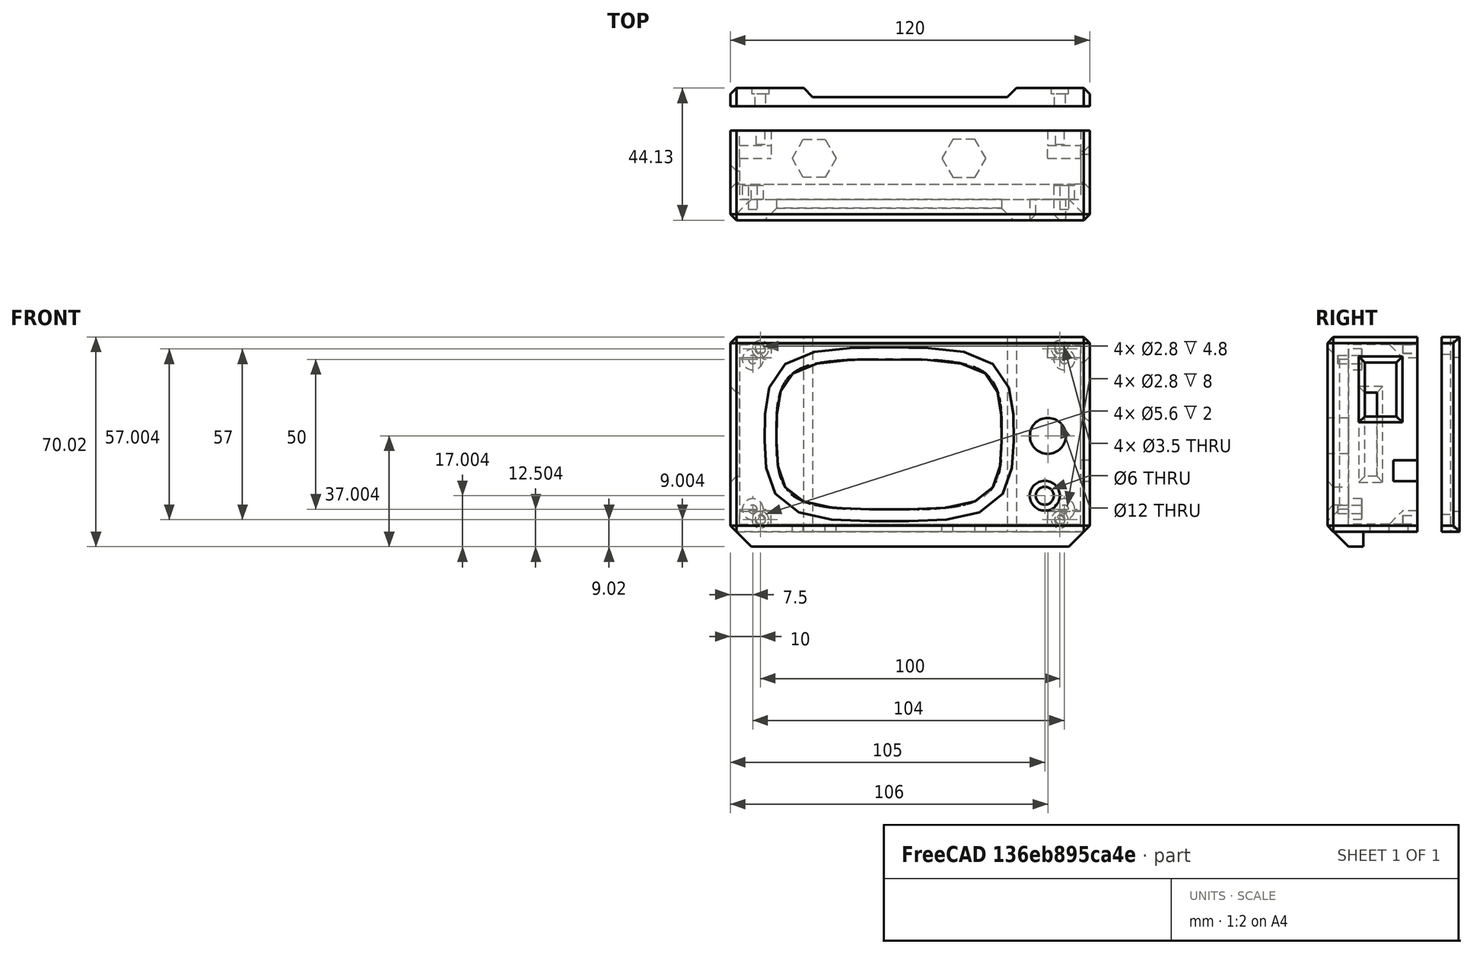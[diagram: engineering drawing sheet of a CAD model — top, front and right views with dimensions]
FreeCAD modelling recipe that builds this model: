
FCSTD DOCUMENT  (FreeCAD 0.19R)
Label: Pendant
License: All rights reserved
LicenseURL: http://en.wikipedia.org/wiki/All_rights_reserved
objects: Sketcher::SketchObject×18, PartDesign::Pocket×12, PartDesign::Chamfer×8, PartDesign::Pad×5, PartDesign::Mirrored×2, PartDesign::Body×2, Mesh::Feature×2
note: 72 computed .brp shape members not serialized (recipe doc carries the construction recipe); baked Part::Feature solids carry a one-line shape summary decoded from their .brp

FEATURE [Sketcher::SketchObject] Sketch028  label="knob"
  FullyConstrained = false
  MapMode = 5
  Placement = pos=(0,0,0) rot=(1,0,0;3.14159rad)
  sketch-geometry (1):
    g0: Circle CenterX=52 CenterY=20.5 CenterZ=0 NormalX=0 NormalY=0 NormalZ=1 AngleXU=0 Radius=3
  constraints (1):
    c: Diameter(g0) = 6
FEATURE [Sketcher::SketchObject] Sketch029
  FullyConstrained = true
  MapMode = 5
  Support = -> [XY_Plane002]
  sketch-geometry (30):
    g0: LineSegment StartX=-53 StartY=32.5 StartZ=0 EndX=67 EndY=32.5 EndZ=0
    g1: LineSegment StartX=67 StartY=32.5 StartZ=0 EndX=67 EndY=-32.5 EndZ=0
    g2: LineSegment StartX=67 StartY=-32.5 StartZ=0 EndX=-53 EndY=-32.5 EndZ=0
    g3: LineSegment StartX=-53 StartY=-32.5 StartZ=0 EndX=-53 EndY=32.5 EndZ=0
    g4: LineSegment StartX=-37 StartY=24.5 StartZ=0 EndX=37 EndY=24.5 EndZ=0
    g5: LineSegment StartX=37 StartY=24.5 StartZ=0 EndX=37 EndY=-24.5 EndZ=0
    g6: LineSegment StartX=37 StartY=-24.5 StartZ=0 EndX=-37 EndY=-24.5 EndZ=0
    g7: LineSegment StartX=-37 StartY=-24.5 StartZ=0 EndX=-37 EndY=24.5 EndZ=0
    g8: LineSegment StartX=-37.7408 StartY=25.116 StartZ=0 EndX=37.7408 EndY=25.116 EndZ=0
    g9: LineSegment StartX=37.7408 StartY=25.116 StartZ=0 EndX=37.7408 EndY=-25.116 EndZ=0
    g10: LineSegment StartX=37.7408 StartY=-25.116 StartZ=0 EndX=-37.7408 EndY=-25.116 EndZ=0
    g11: LineSegment StartX=-37.7408 StartY=-25.116 StartZ=0 EndX=-37.7408 EndY=25.116 EndZ=0
    g12-g19: Circle x8 (B-spline internal-alignment scaffolding for g20; pole/knot coordinates omitted)
    g20: BSplineCurve PolesCount=8 KnotsCount=9 Degree=3 IsPeriodic=1
    g21-g29: GeomPoint x9 (B-spline internal-alignment scaffolding for g20; pole/knot coordinates omitted)
  constraints (53):
    c: Coincident(g0,g1)
    c: Coincident(g1,g2)
    c: Coincident(g2,g3)
    c: Coincident(g3,g0)
    c: Horizontal(g0)
    c: Horizontal(g2)
    c: Vertical(g1)
    c: Vertical(g3)
    c: Coincident(g4,g5)
    c: Coincident(g5,g6)
    c: Coincident(g6,g7)
    c: Coincident(g7,g4)
    c: Horizontal(g4)
    c: Vertical(g7)
    c: Distance(g5) = 49
    c: Distance(g4,g3) = 16
    c: Distance(g0,g5) = 30
    c: Distance(g6,g2) = 8
    c: Distance(g4,g0) = 8
    c: Distance(g6) = 74
    c: Symmetric(g5,g6,g-2)
    c: Symmetric(g5,g4,g-1)
    c: Coincident(g8,g9)
    c: Coincident(g9,g10)
    c: Coincident(g10,g11)
    c: Coincident(g11,g8)
    c: Horizontal(g8)
    c: Horizontal(g10)
    c: Vertical(g9)
    c: Vertical(g11)
    c: Symmetric(g9,g8,g-1)
    c: Weight(g12) = 1
    c: Equal(g12,g13)
    c: Equal(g12,g14)
    c: Equal(g12,g15)
    c: PointOnObject(g15,g-1)
    c: Equal(g12,g16)
    c: Equal(g12,g17)
    c: PointOnObject(g17,g-2)
    c: Equal(g12,g18)
    c: Equal(g12,g19)
    c: InternalAlignment(g12-g19 -> g20) x8
    c: InternalAlignment(g21-g29 -> g20) x9
    c: Coincident(g8,g12)
    c: Coincident(g14,g8)
    c: Coincident(g16,g10)
    c: Coincident(g18,g9)
    c: Distance(g19,g5) = 0.5
    c: Symmetric(g19,g15,g-2)
    c: Distance(g17,g6) = 0.5
    c: Symmetric(g17,g13,g-1)
    c: DistanceX(g8) = 37.7408
    c: DistanceY(g8) = 25.116
FEATURE [PartDesign::Pad] Pad005
  Direction = (1,1,1)
  Length = 30
  Length2 = 100
  Profile = -> Sketch029
  Type = 0
FEATURE [PartDesign::Pocket] Pocket016
  BaseFeature = -> Pad005
  Length = 5
  Length2 = 100
  Profile = -> Sketch028
  Type = 1
FEATURE [Sketcher::SketchObject] Sketch001  label="knob001"
  FullyConstrained = false
  MapMode = 5
  Placement = pos=(0,0,30) rot=(0,0,1;0rad)
  Support = -> [Pocket016]
  sketch-geometry (1):
    g0: Circle CenterX=53 CenterY=-0.5 CenterZ=0 NormalX=0 NormalY=0 NormalZ=1 AngleXU=0 Radius=6
  constraints (2):
    c: Diameter(g0) = 12
    c: DistanceY(g0) = -0.5
FEATURE [PartDesign::Pocket] Pocket017
  BaseFeature = -> Pocket016
  Length = 5
  Length2 = 100
  Profile = -> Sketch001
  Type = 1
FEATURE [Sketcher::SketchObject] Sketch030  label="BodyPocket"
  ExternalGeometry = -> [Pocket017]
  FullyConstrained = true
  MapMode = 5
  Placement = pos=(0,0,0) rot=(1,0,0;3.14159rad)
  Support = -> [Pocket017]
  sketch-geometry (4):
    g0: LineSegment StartX=-50 StartY=30 StartZ=0 EndX=64 EndY=30 EndZ=0
    g1: LineSegment StartX=64 StartY=30 StartZ=0 EndX=64 EndY=-30 EndZ=0
    g2: LineSegment StartX=64 StartY=-30 StartZ=0 EndX=-50 EndY=-30 EndZ=0
    g3: LineSegment StartX=-50 StartY=-30 StartZ=0 EndX=-50 EndY=30 EndZ=0
  constraints (12):
    c: Coincident(g0,g1)
    c: Coincident(g1,g2)
    c: Coincident(g2,g3)
    c: Coincident(g3,g0)
    c: Horizontal(g0)
    c: Horizontal(g2)
    c: Vertical(g1)
    c: DistanceX(g0) = -50
    c: DistanceY(g0) = 30
    c: DistanceX(g1) = 64
    c: DistanceY(g2) = -30
    c: Vertical(g3)
FEATURE [PartDesign::Pocket] Pocket018
  BaseFeature = -> Pocket017
  Length = 23
  Length2 = 100
  Profile = -> Sketch030
  Type = 0
FEATURE [PartDesign::Chamfer] Chamfer001
  Angle = 45
  Base = -> Pocket018 [Edge19]
  BaseFeature = -> Pocket018
  ChamferType = 0
  FlipDirection = false
  Size = 4
  Size2 = 1
  SupportTransform = false
FEATURE [Sketcher::SketchObject] Sketch031  label="standofs"
  FullyConstrained = true
  MapMode = 5
  Placement = pos=(0,0,23) rot=(1,0,0;3.14159rad)
  Support = -> [Chamfer001]
  sketch-geometry (4):
    g0: Circle CenterX=-45.5 CenterY=25 CenterZ=0 NormalX=0 NormalY=0 NormalZ=1 AngleXU=0 Radius=3.5
    g1: Circle CenterX=-45.5 CenterY=-25 CenterZ=0 NormalX=0 NormalY=0 NormalZ=1 AngleXU=0 Radius=3.5
    g2: Circle CenterX=58.5 CenterY=-25 CenterZ=0 NormalX=0 NormalY=0 NormalZ=1 AngleXU=0 Radius=3.5
    g3: Circle CenterX=58.5 CenterY=25 CenterZ=0 NormalX=0 NormalY=0 NormalZ=1 AngleXU=0 Radius=3.5
  constraints (10):
    c: Diameter(g0) = 7
    c: Equal(g0,g1)
    c: Equal(g0,g3)
    c: Equal(g0,g2)
    c: Symmetric(g1,g0,g-1)
    c: Symmetric(g2,g3,g-1)
    c: Distance(g3,g2) = 50
    c: Distance(g1,g0) = 50
    c: Distance(g3,g0) = 104
    c: DistanceX(g0) = -45.5
FEATURE [PartDesign::Pad] Pad006
  BaseFeature = -> Chamfer001
  Direction = (1,1,1)
  Length = 4.5
  Length2 = 100
  Profile = -> Sketch031
  Type = 0
FEATURE [Sketcher::SketchObject] Sketch032  label="holes"
  FullyConstrained = true
  MapMode = 5
  Placement = pos=(0,0,18.5) rot=(1,0,0;3.14159rad)
  Support = -> [Pad006]
  sketch-geometry (4):
    g0: Circle CenterX=-45.5 CenterY=25 CenterZ=0 NormalX=0 NormalY=0 NormalZ=1 AngleXU=0 Radius=1.4
    g1: Circle CenterX=58.5 CenterY=25 CenterZ=0 NormalX=0 NormalY=0 NormalZ=1 AngleXU=0 Radius=1.4
    g2: Circle CenterX=58.5 CenterY=-25 CenterZ=0 NormalX=0 NormalY=0 NormalZ=1 AngleXU=0 Radius=1.4
    g3: Circle CenterX=-45.5 CenterY=-25 CenterZ=0 NormalX=0 NormalY=0 NormalZ=1 AngleXU=0 Radius=1.4
  constraints (10):
    c: Distance(g3,g2) = 104
    c: Distance(g3,g0) = 50
    c: Symmetric(g3,g0,g-1)
    c: Symmetric(g2,g1,g-1)
    c: Diameter(g1) = 2.8
    c: Equal(g1,g2)
    c: Equal(g1,g3)
    c: Equal(g1,g0)
    c: DistanceX(g0) = -45.5
    c: Distance(g1,g2) = 50
FEATURE [PartDesign::Pocket] Pocket019
  BaseFeature = -> Pad006
  Length = 8
  Length2 = 100
  Profile = -> Sketch032
  Type = 0
FEATURE [Sketcher::SketchObject] Sketch033
  ExternalGeometry = -> [Pocket019]
  FullyConstrained = true
  MapMode = 5
  Placement = pos=(67,0,0) rot=(0.57735,0.57735,0.57735;2.0944rad)
  Support = -> [Pocket019]
  sketch-geometry (4):
    g0: LineSegment StartX=6 StartY=17.5 StartZ=0 EndX=24 EndY=17.5 EndZ=0
    g1: LineSegment StartX=24 StartY=17.5 StartZ=0 EndX=24 EndY=7 EndZ=0
    g2: LineSegment StartX=24 StartY=7 StartZ=0 EndX=6 EndY=7 EndZ=0
    g3: LineSegment StartX=6 StartY=7 StartZ=0 EndX=6 EndY=17.5 EndZ=0
  constraints (12):
    c: Coincident(g0,g1)
    c: Coincident(g1,g2)
    c: Coincident(g2,g3)
    c: Coincident(g3,g0)
    c: Horizontal(g0)
    c: Horizontal(g2)
    c: Vertical(g1)
    c: Vertical(g3)
    c: Distance(g-3,g0) = 1
    c: Distance(g0) = 18
    c: Distance(g0,g-4) = 6
    c: DistanceY(g1) = 7
FEATURE [PartDesign::Pocket] Pocket020
  BaseFeature = -> Pocket019
  Length = 9
  Length2 = 100
  Profile = -> Sketch033
  Type = 0
FEATURE [Sketcher::SketchObject] Sketch034  label="SD"
  ExternalGeometry = -> [Pocket020]
  FullyConstrained = true
  MapMode = 5
  Placement = pos=(-53,0,0) rot=(0.57735,-0.57735,-0.57735;2.0944rad)
  Support = -> [Pocket020]
  sketch-geometry (4):
    g0: LineSegment StartX=-14 StartY=17.5 StartZ=0 EndX=14 EndY=17.5 EndZ=0
    g1: LineSegment StartX=14 StartY=17.5 StartZ=0 EndX=14 EndY=13.5 EndZ=0
    g2: LineSegment StartX=14 StartY=13.5 StartZ=0 EndX=-14 EndY=13.5 EndZ=0
    g3: LineSegment StartX=-14 StartY=13.5 StartZ=0 EndX=-14 EndY=17.5 EndZ=0
  constraints (11):
    c: Coincident(g0,g1)
    c: Coincident(g1,g2)
    c: Coincident(g2,g3)
    c: Coincident(g3,g0)
    c: Horizontal(g0)
    c: Vertical(g1)
    c: Vertical(g3)
    c: Distance(g0,g-3) = 1
    c: Distance(g1) = 4
    c: Symmetric(g1,g2,g-2)
    c: Distance(g2) = 28
FEATURE [PartDesign::Pocket] Pocket021
  BaseFeature = -> Pocket020
  Length = 5
  Length2 = 100
  Profile = -> Sketch034
  Type = 0
FEATURE [PartDesign::Chamfer] Chamfer
  Angle = 45
  Base = -> Pocket021 [Edge13,Edge3,Edge5,Edge10,Edge2,Edge11,Edge4,Edge20]
  BaseFeature = -> Pocket021
  ChamferType = 0
  FlipDirection = false
  Size = 2
  Size2 = 1
  SupportTransform = false
FEATURE [PartDesign::Chamfer] Chamfer002
  Angle = 45
  Base = -> Chamfer [Edge6]
  BaseFeature = -> Chamfer
  ChamferType = 0
  FlipDirection = false
  Size = 2
  Size2 = 1
  SupportTransform = false
FEATURE [PartDesign::Chamfer] Chamfer003
  Angle = 45
  Base = -> Chamfer002 [Edge50,Edge51,Edge48,Edge49]
  BaseFeature = -> Chamfer002
  ChamferType = 0
  FlipDirection = false
  Size = 2
  Size2 = 1
  SupportTransform = false
FEATURE [PartDesign::Chamfer] Chamfer004
  Angle = 45
  Base = -> Chamfer003 [Edge52,Edge50,Edge49,Edge51]
  BaseFeature = -> Chamfer003
  ChamferType = 0
  FlipDirection = false
  Size = 2
  Size2 = 1
  SupportTransform = false
FEATURE [Sketcher::SketchObject] Sketch
  FullyConstrained = true
  MapMode = 5
  Placement = pos=(0,0,0) rot=(1,0,0;1.5708rad)
  Support = -> [XZ_Plane003]
  sketch-geometry (4):
    g0: LineSegment StartX=60 StartY=32.5 StartZ=0 EndX=-60 EndY=32.5 EndZ=0
    g1: LineSegment StartX=-60 StartY=32.5 StartZ=0 EndX=-60 EndY=-32.5 EndZ=0
    g2: LineSegment StartX=-60 StartY=-32.5 StartZ=0 EndX=60 EndY=-32.5 EndZ=0
    g3: LineSegment StartX=60 StartY=-32.5 StartZ=0 EndX=60 EndY=32.5 EndZ=0
  constraints (11):
    c: Coincident(g0,g1)
    c: Coincident(g1,g2)
    c: Coincident(g2,g3)
    c: Coincident(g3,g0)
    c: Horizontal(g0)
    c: Horizontal(g2)
    c: Vertical(g1)
    c: Vertical(g3)
    c: Symmetric(g1,g0,g-1)
    c: Distance(g0) = 120
    c: Distance(g3) = 65
FEATURE [PartDesign::Pad] Pad007
  Direction = (1,1,1)
  Length = 6
  Length2 = 100
  Placement = pos=(0,0,0) rot=(1,0,0;1.5708rad)
  Profile = -> Sketch
  Type = 0
FEATURE [Sketcher::SketchObject] Sketch054
  FullyConstrained = false
  MapMode = 5
  Placement = pos=(0,-7.2e-15,32.5) rot=(0,0,1;3.14159rad)
  Support = -> [Pad007]
  sketch-geometry (10):
    g0: LineSegment StartX=-73.6086 StartY=-3.6695 StartZ=0 EndX=-50.8099 EndY=-15.0772 EndZ=0
    g1: LineSegment StartX=-50.8099 StartY=-15.0772 StartZ=0 EndX=-50.5772 EndY=-15.0772 EndZ=0
    g2: LineSegment StartX=-50.5772 StartY=-15.0772 StartZ=0 EndX=-32.5 EndY=3 EndZ=0
    g3: LineSegment StartX=-32.5 StartY=3 StartZ=0 EndX=32.5 EndY=3 EndZ=0
    g4: LineSegment StartX=32.5 StartY=3 StartZ=0 EndX=50.5772 EndY=-15.0772 EndZ=0
    g5: LineSegment StartX=50.5772 StartY=-15.0772 StartZ=0 EndX=50.8099 EndY=-15.0772 EndZ=0
    g6: LineSegment StartX=50.8099 StartY=-15.0772 StartZ=0 EndX=73.6086 EndY=-3.6695 EndZ=0
    g7: LineSegment StartX=73.6086 StartY=-3.6695 StartZ=0 EndX=73.6086 EndY=-24.4589 EndZ=0
    g8: LineSegment StartX=73.6086 StartY=-24.4589 StartZ=0 EndX=-87.2751 EndY=-33.7373 EndZ=0
    g9: LineSegment StartX=-87.2751 StartY=-33.7373 StartZ=0 EndX=-73.6086 EndY=-3.6695 EndZ=0
  constraints (19):
    c: Coincident(g0,g1)
    c: Horizontal(g1)
    c: Coincident(g1,g2)
    c: Coincident(g2,g3)
    c: Coincident(g3,g4)
    c: Coincident(g4,g5)
    c: Coincident(g5,g6)
    c: Coincident(g6,g7)
    c: Vertical(g7)
    c: Coincident(g7,g8)
    c: Coincident(g8,g9)
    c: Coincident(g9,g0)
    c: Symmetric(g2,g3,g-2)
    c: Symmetric(g1,g4,g-2)
    c: Symmetric(g0,g5,g-2)
    c: Symmetric(g0,g6,g-2)
    c: DistanceY(g3) = 3
    c: Angle(g2) = 0.785398
    c: Distance(g3) = 65
FEATURE [Sketcher::SketchObject] Sketch055
  FullyConstrained = false
  MapMode = 5
  Placement = pos=(0,0,0) rot=(-1,0,0;1.5708rad)
  sketch-geometry (4):
    g0: Circle CenterX=-50 CenterY=28.5 CenterZ=0 NormalX=0 NormalY=0 NormalZ=1 AngleXU=0 Radius=1.75
    g1: Circle CenterX=-50 CenterY=-28.5 CenterZ=0 NormalX=0 NormalY=0 NormalZ=1 AngleXU=0 Radius=1.75
    g2: Circle CenterX=50 CenterY=28.5 CenterZ=0 NormalX=0 NormalY=0 NormalZ=1 AngleXU=0 Radius=1.75
    g3: Circle CenterX=50 CenterY=-28.5 CenterZ=0 NormalX=0 NormalY=0 NormalZ=1 AngleXU=0 Radius=1.75
  constraints (8):
    c: Symmetric(g0,g1,g-1)
    c: Symmetric(g3,g2,g-1)
    c: Symmetric(g2,g0,g-2)
    c: Diameter(g0) = 3.5
    c: Equal(g0,g1)
    c: Equal(g0,g3)
    c: Equal(g0,g2)
    c: DistanceX(g0) = -50
FEATURE [Sketcher::SketchObject] Sketch056
  FullyConstrained = false
  MapMode = 5
  Placement = pos=(0,0,0) rot=(1,0,0;3.14159rad)
  Support = -> [Chamfer004]
  sketch-geometry (12):
    g0: Circle CenterX=-43 CenterY=28.5 CenterZ=0 NormalX=0 NormalY=0 NormalZ=1 AngleXU=0 Radius=1.4
    g1: Circle CenterX=-43 CenterY=-28.5 CenterZ=0 NormalX=0 NormalY=0 NormalZ=1 AngleXU=0 Radius=1.4
    g2: Circle CenterX=57 CenterY=-28.5 CenterZ=0 NormalX=0 NormalY=0 NormalZ=1 AngleXU=0 Radius=1.4
    g3: Circle CenterX=57 CenterY=28.5 CenterZ=0 NormalX=0 NormalY=0 NormalZ=1 AngleXU=0 Radius=1.4
    g4: LineSegment StartX=-50.6829 StartY=31.3269 StartZ=0 EndX=-39.4314 EndY=31.3269 EndZ=0
    g5: LineSegment StartX=-39.4314 StartY=31.3269 StartZ=0 EndX=-39.4314 EndY=25.5 EndZ=0
    g6: LineSegment StartX=-39.4314 StartY=25.5 StartZ=0 EndX=-50.6829 EndY=25.5 EndZ=0
    g7: LineSegment StartX=-50.6829 StartY=25.5 StartZ=0 EndX=-50.6829 EndY=31.3269 EndZ=0
    g8: LineSegment StartX=52.9243 StartY=31.27 StartZ=0 EndX=65.0031 EndY=31.27 EndZ=0
    g9: LineSegment StartX=65.0031 StartY=31.27 StartZ=0 EndX=65.0031 EndY=25.5 EndZ=0
    g10: LineSegment StartX=65.0031 StartY=25.5 StartZ=0 EndX=52.9243 EndY=25.5 EndZ=0
    g11: LineSegment StartX=52.9243 StartY=25.5 StartZ=0 EndX=52.9243 EndY=31.27 EndZ=0
  constraints (29):
    c: Diameter(g0) = 2.8
    c: Equal(g0,g1)
    c: Equal(g0,g2)
    c: Equal(g0,g3)
    c: DistanceX(g1) = -43
    c: DistanceY(g1) = -28.5
    c: DistanceX(g0) = -43
    c: DistanceY(g0) = 28.5
    c: DistanceX(g3) = 57
    c: DistanceY(g3) = 28.5
    c: Symmetric(g2,g3,g-1)
    c: Coincident(g4,g5)
    c: Coincident(g5,g6)
    c: Coincident(g6,g7)
    c: Coincident(g7,g4)
    c: Horizontal(g4)
    c: Horizontal(g6)
    c: Vertical(g5)
    c: Vertical(g7)
    c: Coincident(g8,g9)
    c: Coincident(g9,g10)
    c: Coincident(g10,g11)
    c: Coincident(g11,g8)
    c: Horizontal(g8)
    c: Horizontal(g10)
    c: Vertical(g9)
    c: Vertical(g11)
    c: DistanceY(g5) = 25.5
    c: DistanceY(g10) = 25.5
FEATURE [PartDesign::Pad] Pad008
  BaseFeature = -> Chamfer004
  Direction = (1,1,1)
  Length = 5
  Length2 = 100
  Profile = -> Sketch056
  Reversed = true
  Type = 0
FEATURE [PartDesign::Mirrored] Mirrored
  BaseFeature = -> Pad008
  MirrorPlane = -> Sketch056 [H_Axis]
  Originals = -> [Pad008]
FEATURE [Sketcher::SketchObject] Sketch058
  FullyConstrained = false
  MapMode = 5
  Placement = pos=(0,0,0) rot=(1,0,0;3.14159rad)
  sketch-geometry (4):
    g0: Circle CenterX=-43 CenterY=28.5 CenterZ=0 NormalX=0 NormalY=0 NormalZ=1 AngleXU=0 Radius=1.4
    g1: Circle CenterX=-43 CenterY=-28.5039 CenterZ=0 NormalX=0 NormalY=0 NormalZ=1 AngleXU=0 Radius=1.4
    g2: Circle CenterX=57 CenterY=-28.5 CenterZ=0 NormalX=0 NormalY=0 NormalZ=1 AngleXU=0 Radius=1.4
    g3: Circle CenterX=57 CenterY=28.5 CenterZ=0 NormalX=0 NormalY=0 NormalZ=1 AngleXU=0 Radius=1.4
  constraints (11):
    c: DistanceX(g3) = 57
    c: DistanceY(g3) = 28.5
    c: DistanceY(g2) = -28.5
    c: DistanceX(g2) = 57
    c: DistanceX(g1) = -43
    c: DistanceY(g0) = 28.5
    c: DistanceX(g0) = -43
    c: Diameter(g0) = 2.8
    c: Equal(g0,g1)
    c: Equal(g0,g2)
    c: Equal(g0,g3)
FEATURE [PartDesign::Pocket] Pocket038
  BaseFeature = -> Mirrored
  Length = 4.8
  Length2 = 100
  Profile = -> Sketch058
  Type = 0
FEATURE [Sketcher::SketchObject] Sketch057  label="cable"
  FullyConstrained = false
  MapMode = 5
  Placement = pos=(67,0,0) rot=(0.57735,0.57735,0.57735;2.0944rad)
  Support = -> [Pocket038]
  sketch-geometry (4):
    g0: LineSegment StartX=-15.6699 StartY=8 StartZ=0 EndX=-8.66993 EndY=8 EndZ=0
    g1: LineSegment StartX=-8.66993 StartY=8 StartZ=0 EndX=-8.66993 EndY=-1 EndZ=0
    g2: LineSegment StartX=-8.66993 StartY=-1 StartZ=0 EndX=-15.6699 EndY=-1 EndZ=0
    g3: LineSegment StartX=-15.6699 StartY=-1 StartZ=0 EndX=-15.6699 EndY=8 EndZ=0
  constraints (11):
    c: Coincident(g0,g1)
    c: Coincident(g1,g2)
    c: Coincident(g2,g3)
    c: Coincident(g3,g0)
    c: Horizontal(g2)
    c: Vertical(g1)
    c: Vertical(g3)
    c: Distance(g1) = 9
    c: Distance(g0) = 7
    c: DistanceY(g1) = -1
    c: Horizontal(g0)
FEATURE [PartDesign::Pocket] Pocket039
  BaseFeature = -> Pocket038
  Length = 5
  Length2 = 100
  Profile = -> Sketch057
  Type = 0
FEATURE [PartDesign::Pocket] Pocket
  BaseFeature = -> Pad007
  Length = 5
  Length2 = 100
  Placement = pos=(0,0,0) rot=(1,0,0;1.5708rad)
  Profile = -> Sketch054
  Type = 1
FEATURE [PartDesign::Chamfer] Chamfer009
  Angle = 45
  Base = -> Pocket [Edge24,Edge8,Edge9,Edge20,Edge19,Edge6]
  BaseFeature = -> Pocket
  ChamferType = 0
  FlipDirection = false
  Placement = pos=(0,0,0) rot=(1,0,0;1.5708rad)
  Size = 2
  Size2 = 1
  SupportTransform = false
FEATURE [PartDesign::Pocket] Pocket040
  BaseFeature = -> Chamfer009
  Length = 5
  Length2 = 100
  Placement = pos=(0,0,0) rot=(1,0,0;1.5708rad)
  Profile = -> Sketch055
  Type = 1
FEATURE [Sketcher::SketchObject] Sketch059
  ExternalGeometry = -> [Pocket040]
  FullyConstrained = true
  MapMode = 5
  Placement = pos=(0,0,0) rot=(-1,0,0;1.5708rad)
  Support = -> [Pocket040]
  sketch-geometry (4):
    g0: Circle CenterX=-50 CenterY=28.5 CenterZ=0 NormalX=0 NormalY=0 NormalZ=1 AngleXU=0 Radius=2.8
    g1: Circle CenterX=-50 CenterY=-28.5 CenterZ=0 NormalX=0 NormalY=0 NormalZ=1 AngleXU=0 Radius=2.8
    g2: Circle CenterX=50 CenterY=28.5 CenterZ=0 NormalX=0 NormalY=0 NormalZ=1 AngleXU=0 Radius=2.8
    g3: Circle CenterX=50 CenterY=-28.5 CenterZ=0 NormalX=0 NormalY=0 NormalZ=1 AngleXU=0 Radius=2.8
  constraints (8):
    c: Diameter(g0) = 5.6
    c: Equal(g0,g1)
    c: Equal(g0,g2)
    c: Equal(g0,g3)
    c: Coincident(g2,g-6)
    c: Coincident(g0,g-3)
    c: Coincident(g1,g-4)
    c: Coincident(g3,g-5)
FEATURE [PartDesign::Pocket] Pocket041
  BaseFeature = -> Pocket040
  Length = 2
  Length2 = 100
  Placement = pos=(0,0,0) rot=(1,0,0;1.5708rad)
  Profile = -> Sketch059
  Type = 0
FEATURE [PartDesign::Body] Body003  label="BackPanel"
  Group = -> [Sketch,Pad007,Sketch054,Sketch055,Pocket,Chamfer009,Pocket040,Sketch059,Pocket041]
  Origin = -> Origin003
  Placement = pos=(0,14.15,0) rot=(0,0,1;0rad)
  Tip = -> Pocket041
FEATURE [Sketcher::SketchObject] Sketch065
  ExternalGeometry = -> [Pocket039]
  FullyConstrained = true
  MapMode = 5
  Placement = pos=(-39.4314,0,0) rot=(0.57735,0.57735,0.57735;2.0944rad)
  Support = -> [Pocket039]
  sketch-geometry (4):
    g0: LineSegment StartX=-32.5 StartY=28 StartZ=0 EndX=-37.5 EndY=23 EndZ=0
    g1: LineSegment StartX=-37.5 StartY=23 StartZ=0 EndX=-37.5 EndY=18 EndZ=0
    g2: LineSegment StartX=-37.5 StartY=18 StartZ=0 EndX=-32.5 EndY=18 EndZ=0
    g3: LineSegment StartX=-32.5 StartY=18 StartZ=0 EndX=-32.5 EndY=28 EndZ=0
  constraints (11):
    c: Coincident(g0,g1)
    c: Vertical(g1)
    c: Coincident(g1,g2)
    c: Horizontal(g2)
    c: Coincident(g2,g3)
    c: Coincident(g3,g0)
    c: Angle(g0) = -2.35619
    c: Coincident(g0,g-3)
    c: Vertical(g3)
    c: Distance(g2) = 5
    c: Distance(g1) = 5
FEATURE [PartDesign::Pad] Pad
  BaseFeature = -> Pocket039
  Direction = (1,1,1)
  Length = 104.43
  Length2 = 11.55
  Profile = -> Sketch065
  Type = 4
FEATURE [PartDesign::Chamfer] Chamfer010
  Angle = 45
  Base = -> Pad [Edge135,Edge140]
  BaseFeature = -> Pad
  ChamferType = 0
  FlipDirection = false
  Size = 4.98
  Size2 = 1
  SupportTransform = false
FEATURE [Sketcher::SketchObject] Sketch064  label="magnet"
  FullyConstrained = true
  MapMode = 5
  Placement = pos=(0,-32.5,0) rot=(1,0,0;1.5708rad)
  Support = -> [Chamfer010]
  sketch-geometry (7):
    g0: LineSegment StartX=-21.3338 StartY=3 StartZ=0 EndX=-17.6677 EndY=9.35 EndZ=0
    g1: LineSegment StartX=-17.6677 StartY=9.35 StartZ=0 EndX=-21.3338 EndY=15.7 EndZ=0
    g2: LineSegment StartX=-21.3338 StartY=15.7 StartZ=0 EndX=-28.6662 EndY=15.7 EndZ=0
    g3: LineSegment StartX=-28.6662 StartY=15.7 StartZ=0 EndX=-32.3323 EndY=9.35 EndZ=0
    g4: LineSegment StartX=-32.3323 StartY=9.35 StartZ=0 EndX=-28.6662 EndY=3 EndZ=0
    g5: LineSegment StartX=-28.6662 StartY=3 StartZ=0 EndX=-21.3338 EndY=3 EndZ=0
    g6: Circle CenterX=-25 CenterY=9.35 CenterZ=0 NormalX=0 NormalY=0 NormalZ=1 AngleXU=0 Radius=7.33235
  constraints (17):
    c: Coincident(g0,g1)
    c: Coincident(g1,g2)
    c: Coincident(g2,g3)
    c: Coincident(g3,g4)
    c: Coincident(g4,g5)
    c: Coincident(g5,g0)
    c: Equal(g0, g1-g5) x5
    c: PointOnObject(g0,g6)
    c: PointOnObject(g1,g6)
    c: PointOnObject(g2,g6)
    c: PointOnObject(g3,g6)
    c: PointOnObject(g4,g6)
    c: PointOnObject(g5,g6)
    c: Distance(g0,g4) = 12.7
    c: Horizontal(g5)
    c: DistanceX(g6) = -25
    c: DistanceY(g0) = 3
FEATURE [Sketcher::SketchObject] Sketch066
  FullyConstrained = true
  MapMode = 5
  Placement = pos=(0,-32.5,0) rot=(1,0,0;1.5708rad)
  Support = -> [Chamfer010]
FEATURE [PartDesign::Pocket] Pocket042
  BaseFeature = -> Chamfer010
  Length = 2
  Length2 = 100
  Profile = -> Sketch064
  Type = 0
FEATURE [PartDesign::Mirrored] Mirrored001
  BaseFeature = -> Pocket042
  MirrorPlane = -> Sketch064 [V_Axis]
  Originals = -> [Pocket042]
FEATURE [PartDesign::Chamfer] Chamfer011
  Angle = 45
  Base = -> Mirrored001 [Edge140,Edge143,Edge160,Edge163]
  BaseFeature = -> Mirrored001
  ChamferType = 0
  FlipDirection = false
  Size = 4.3
  Size2 = 1
  SupportTransform = false
FEATURE [PartDesign::Body] Body002  label="ScreenBox"
  Group = -> [Sketch029,Pad005,Sketch001,Sketch028,Pocket016,Pocket017,Sketch030,Pocket018,Chamfer001,Sketch031,Pad006,Sketch032,Pocket019,Sketch033,Pocket020,Sketch034,Pocket021,Chamfer,Chamfer002,Chamfer003,Chamfer004,Sketch056,Pad008,Mirrored,Sketch057,Sketch058,Pocket038,Pocket039,Sketch064,Sketch065,Pad,Chamfer010,Sketch066,Pocket042,Mirrored001,Chamfer011]
  Origin = -> Origin002
  Placement = pos=(-7,0.0221075,-0.0158419) rot=(1,0,0;1.5708rad)
  Tip = -> Chamfer011
FEATURE [Mesh::Feature] Mesh  label="Pocket041 (Meshed)"
FEATURE [Mesh::Feature] Mesh001  label="Chamfer011 (Meshed)"
